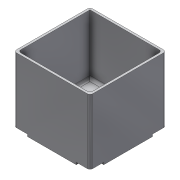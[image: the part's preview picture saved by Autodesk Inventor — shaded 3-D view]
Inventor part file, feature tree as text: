
AUTODESK INVENTOR PART (.ipt)
format: ipt  version: 2021 (Build 250183000, 183)  size: 146,944 bytes
history: native  units: mm
features: extrude x3, sketch x3, other x1, fillet x1, projected_geometry x1
ambient origin geometry x8: Origin, YZ Plane, XZ Plane, XY Plane, X Axis, Y Axis, Z Axis, Center Point
bodies: Body1 (feature_tree)
feature tree (9):
  other  "Твердое тело1"
  extrude  "Выдавливание1"  Depth=141.0mm
  extrude  "Выдавливание2"  Depth=120.0mm TaperAngle=0.0deg
  fillet  "Сопряжение1"  Radius=4.0mm
  extrude  "Выдавливание3"  Depth=110.0mm TaperAngle=0.0deg
  sketch  "Эскиз1"
  sketch  "Эскиз2"
  sketch  "Эскиз3"
  projected_geometry  "Спроецированная петля1"
